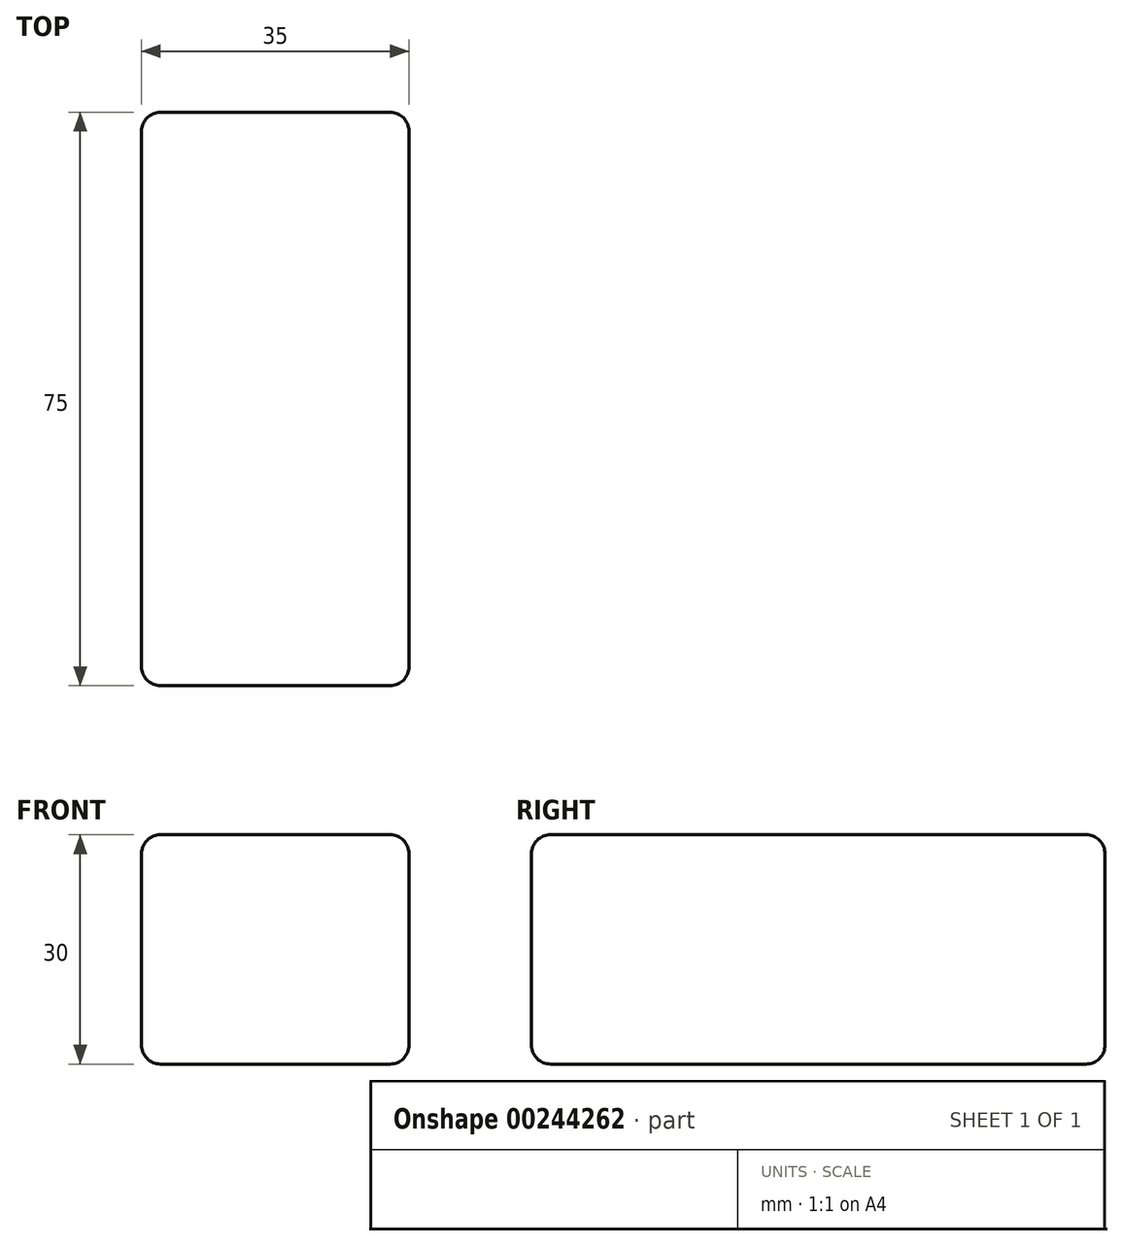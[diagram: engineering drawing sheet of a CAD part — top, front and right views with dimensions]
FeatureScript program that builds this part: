
annotation { "Feature Type Name" : "Feature", "Feature Type Description" : "" }
export const myFeature = defineFeature(function(context is Context, id is Id, definition is map)
    precondition{}
    {
        {
            var Q0;
            Q0=qCreatedBy(makeId("Top.planeOp"),FACE);
            var sketch = newSketch(context, id + "F0", { "sketchPlane" : qUnion([Q0])});
            skLineSegment(sketch, "E0.bottom", {"start": v(17.5, 37.5) * mm, "end": v(-17.5, 37.5) * mm});
            skLineSegment(sketch, "E0.top", {"start": v(17.5, -37.5) * mm, "end": v(-17.5, -37.5) * mm});
            skLineSegment(sketch, "E0.left", {"start": v(17.5, 37.5) * mm, "end": v(17.5, -37.5) * mm});
            skLineSegment(sketch, "E0.right", {"start": v(-17.5, 37.5) * mm, "end": v(-17.5, -37.5) * mm});
            skPoint(sketch, "E0.middle", {"position": v(0, 0) * mm});
            skSolve(sketch);
        }
        {
            var Q0;
            Q0=qSketchRegion(id+"F0",true);
            extrude(context, id + "F1", {"entities" : qUnion([Q0]), "depth" : 30 * mm});
        }
        {
            var Q0;
            Q0=makeQuery(id+"F1.opExtrude","CAP_EDGE",EDGE,{"disambiguationData":[OSD([sQuery(id+"F0.wireOp",EDGE,"E0.bottom")])],"isStart":false});
            var Q1;
            Q1=makeQuery(id+"F1.opExtrude","CAP_EDGE",EDGE,{"disambiguationData":[OSD([sQuery(id+"F0.wireOp",EDGE,"E0.right")])],"isStart":false});
            var Q2;
            Q2=makeQuery(id+"F1.opExtrude","CAP_EDGE",EDGE,{"disambiguationData":[OSD([sQuery(id+"F0.wireOp",EDGE,"E0.top")])],"isStart":false});
            var Q3;
            Q3=makeQuery(id+"F1.opExtrude","CAP_EDGE",EDGE,{"disambiguationData":[OSD([sQuery(id+"F0.wireOp",EDGE,"E0.left")])],"isStart":false});
            var Q4;
            Q4=makeQuery(id+"F1.opExtrude","SWEPT_EDGE",EDGE,{"disambiguationData":[OSD([sQuery(id+"F0.wireOp",EDGE,"E0.top"),sQuery(id+"F0.wireOp",EDGE,"E0.left")])]});
            var Q5;
            Q5=makeQuery(id+"F1.opExtrude","SWEPT_EDGE",EDGE,{"disambiguationData":[OSD([sQuery(id+"F0.wireOp",EDGE,"E0.top"),sQuery(id+"F0.wireOp",EDGE,"E0.right")])]});
            var Q6;
            Q6=makeQuery(id+"F1.opExtrude","CAP_EDGE",EDGE,{"disambiguationData":[OSD([sQuery(id+"F0.wireOp",EDGE,"E0.top")])],"isStart":true});
            var Q7;
            Q7=makeQuery(id+"F1.opExtrude","CAP_EDGE",EDGE,{"disambiguationData":[OSD([sQuery(id+"F0.wireOp",EDGE,"E0.left")])],"isStart":true});
            var Q8;
            Q8=makeQuery(id+"F1.opExtrude","SWEPT_EDGE",EDGE,{"disambiguationData":[OSD([sQuery(id+"F0.wireOp",EDGE,"E0.bottom"),sQuery(id+"F0.wireOp",EDGE,"E0.left")])]});
            var Q9;
            Q9=makeQuery(id+"F1.opExtrude","CAP_EDGE",EDGE,{"disambiguationData":[OSD([sQuery(id+"F0.wireOp",EDGE,"E0.bottom")])],"isStart":true});
            var Q10;
            Q10=makeQuery(id+"F1.opExtrude","CAP_EDGE",EDGE,{"disambiguationData":[OSD([sQuery(id+"F0.wireOp",EDGE,"E0.right")])],"isStart":true});
            var Q11;
            Q11=makeQuery(id+"F1.opExtrude","SWEPT_EDGE",EDGE,{"disambiguationData":[OSD([sQuery(id+"F0.wireOp",EDGE,"E0.bottom"),sQuery(id+"F0.wireOp",EDGE,"E0.right")])]});
            fillet(context, id + "F2", {"entities" : qUnion([Q0, Q1, Q2, Q3, Q4, Q5, Q6, Q7, Q8, Q9, Q10, Q11]), "radius" : 2.5 * mm, "tangentPropagation" : true, "allowEdgeOverflow" : false});
        }
    });
